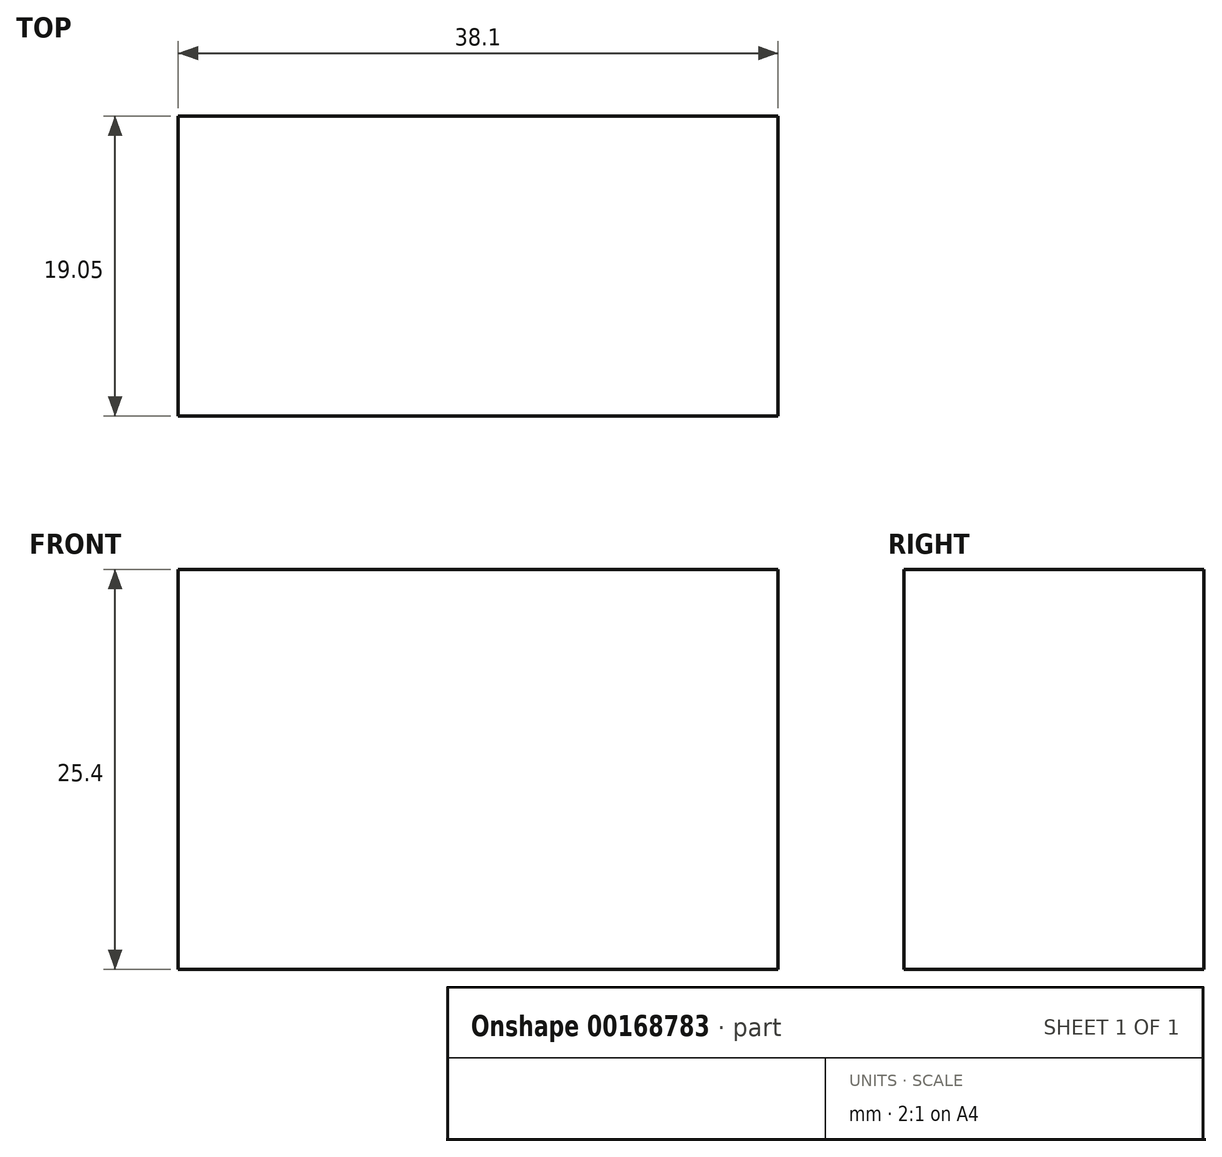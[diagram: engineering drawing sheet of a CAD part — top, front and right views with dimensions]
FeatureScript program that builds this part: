
annotation { "Feature Type Name" : "Feature", "Feature Type Description" : "" }
export const myFeature = defineFeature(function(context is Context, id is Id, definition is map)
    precondition{}
    {
        {
            var Q0;
            Q0=qCreatedBy(makeId("Front.planeOp"),FACE);
            var sketch = newSketch(context, id + "F0", { "sketchPlane" : qUnion([Q0])});
            skLineSegment(sketch, "E0.bottom", {"start": v(19.05, -12.7) * mm, "end": v(-19.05, -12.7) * mm});
            skLineSegment(sketch, "E0.top", {"start": v(19.05, 12.7) * mm, "end": v(-19.05, 12.7) * mm});
            skLineSegment(sketch, "E0.left", {"start": v(19.05, -12.7) * mm, "end": v(19.05, 12.7) * mm});
            skLineSegment(sketch, "E0.right", {"start": v(-19.05, -12.7) * mm, "end": v(-19.05, 12.7) * mm});
            skPoint(sketch, "E0.middle", {"position": v(0, 0) * mm});
            skSolve(sketch);
        }
        {
            var Q0;
            Q0 = qSketchRegion(id + "F0", true);
            extrude(context, id + "F1", {"entities" : qUnion([Q0]), "depth" : 19.05 * mm});
        }
    });
